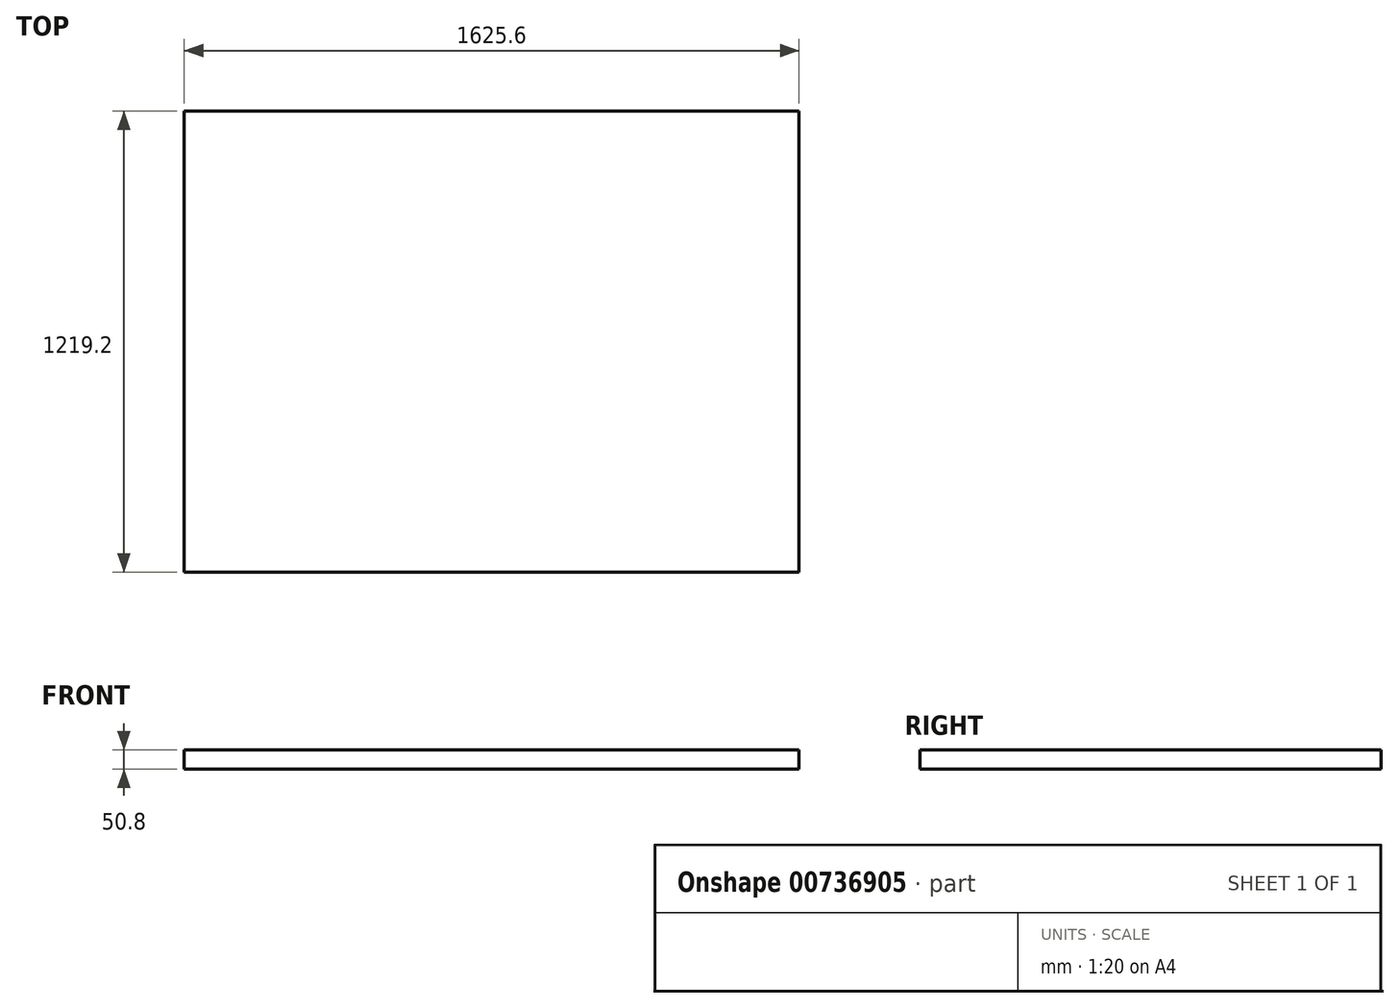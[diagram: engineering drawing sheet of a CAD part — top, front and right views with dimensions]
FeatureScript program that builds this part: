
annotation { "Feature Type Name" : "Feature", "Feature Type Description" : "" }
export const myFeature = defineFeature(function(context is Context, id is Id, definition is map)
    precondition{}
    {
        {
            var Q0;
            Q0=qCreatedBy(makeId("Top.planeOp"),FACE);
            var sketch = newSketch(context, id + "F0", { "sketchPlane" : qUnion([Q0])});
            skLineSegment(sketch, "E0.bottom", {"start": v(0, 0) * mm, "end": v(1625.6, 0) * mm});
            skLineSegment(sketch, "E0.top", {"start": v(0, 1219.2) * mm, "end": v(1625.6, 1219.2) * mm});
            skLineSegment(sketch, "E0.left", {"start": v(0, 0) * mm, "end": v(0, 1219.2) * mm});
            skLineSegment(sketch, "E0.right", {"start": v(1625.6, 0) * mm, "end": v(1625.6, 1219.2) * mm});
            skSolve(sketch);
        }
        {
            var Q0;
            Q0=makeQuery(id+"F0.imprint","IMPRINT",FACE,{"disambiguationData":[TD([[makeQuery(id+"F0.imprint","IMPRINT",EDGE,{"derivedFrom":sQuery(id+"F0.wireOp",EDGE,"E0.bottom")}),1.0]])]});
            extrude(context, id + "F1", {"entities" : qUnion([Q0]), "depth" : 50.8 * mm, "offsetDistance" : 25.4 * mm});
        }
    });
